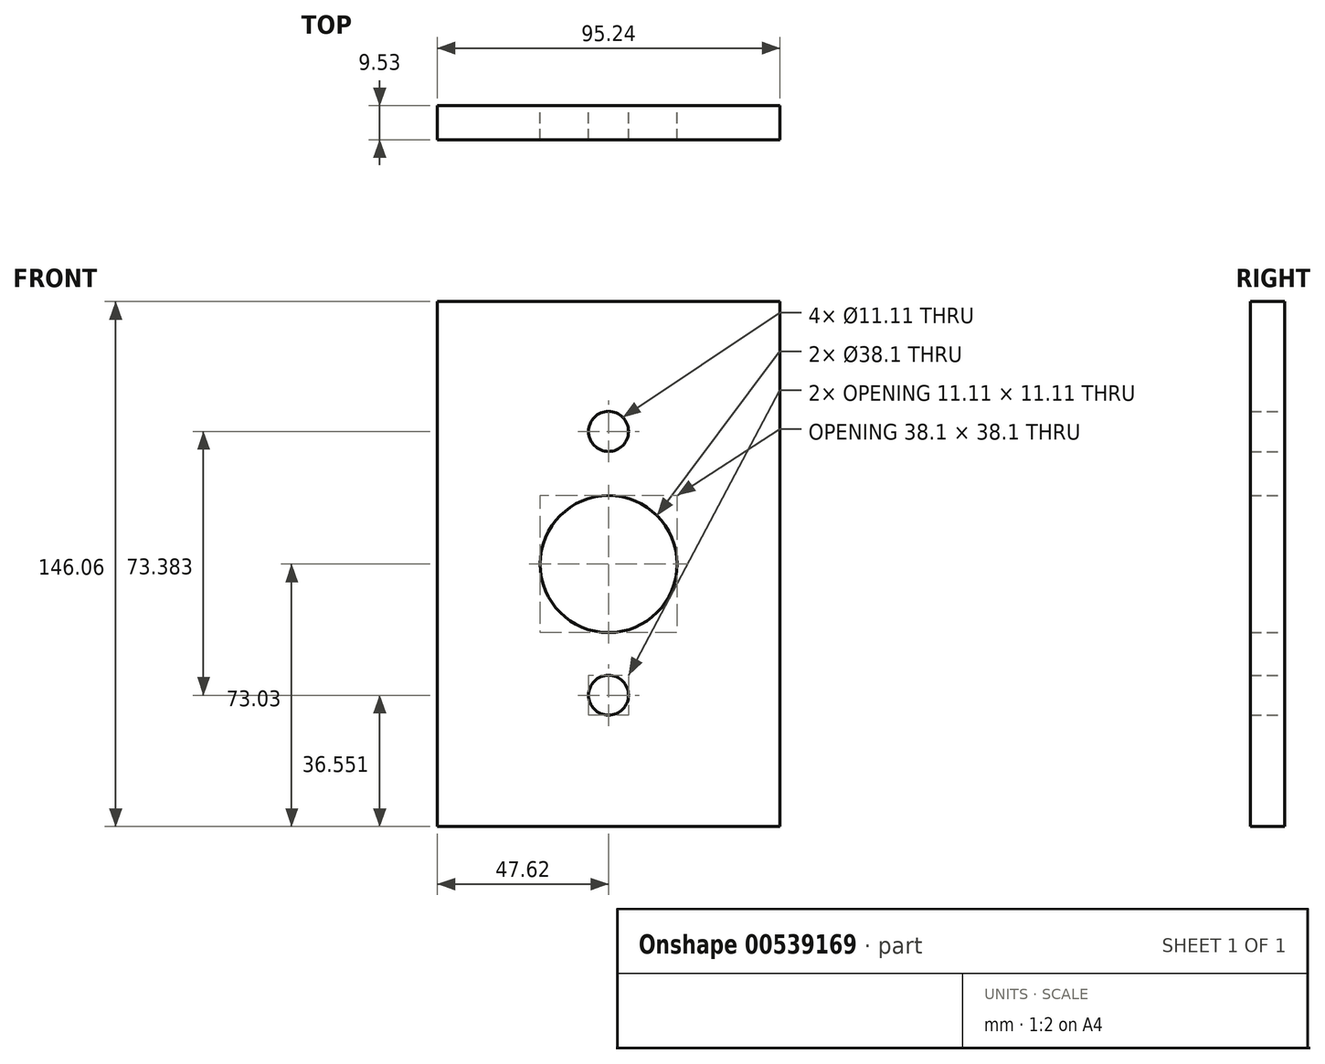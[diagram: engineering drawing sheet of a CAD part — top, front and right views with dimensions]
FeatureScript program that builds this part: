
annotation { "Feature Type Name" : "Feature", "Feature Type Description" : "" }
export const myFeature = defineFeature(function(context is Context, id is Id, definition is map)
    precondition{}
    {
        {
            var Q0;
            Q0=qCreatedBy(makeId("Front.planeOp"),FACE);
            var sketch = newSketch(context, id + "F0", { "sketchPlane" : qUnion([Q0])});
            skCircle(sketch, "E0", {"center": v(0, 0) * mm, "radius": 19.05 * mm});
            skCircle(sketch, "E1", {"center": v(0, 36.9) * mm, "radius": 5.56 * mm});
            skCircle(sketch, "E2", {"center": v(0, -36.48) * mm, "radius": 5.56 * mm});
            skSolve(sketch);
        }
        {
            var Q0;
            Q0=qCreatedBy(makeId("Front.planeOp"),FACE);
            var sketch = newSketch(context, id + "F1", { "sketchPlane" : qUnion([Q0])});
            skLineSegment(sketch, "E3.bottom", {"start": v(-47.62, 73.02) * mm, "end": v(47.63, 73.02) * mm});
            skLineSegment(sketch, "E3.top", {"start": v(-47.63, -73.03) * mm, "end": v(47.62, -73.03) * mm});
            skLineSegment(sketch, "E3.left", {"start": v(-47.62, 73.02) * mm, "end": v(-47.63, -73.03) * mm});
            skLineSegment(sketch, "E3.right", {"start": v(47.63, 73.02) * mm, "end": v(47.62, -73.03) * mm});
            skPoint(sketch, "E3.middle", {"position": v(0, 0) * mm});
            skSolve(sketch);
        }
        {
            var Q0;
            Q0=makeQuery(id+"F1.imprint","IMPRINT",FACE,{"disambiguationData":[TD([[makeQuery(id+"F1.imprint","IMPRINT",EDGE,{"derivedFrom":sQuery(id+"F1.wireOp",EDGE,"E3.bottom")}),-1.0]])]});
            extrude(context, id + "F2", {"entities" : qUnion([Q0]), "depth" : 9.52 * mm, "offsetDistance" : 25.4 * mm});
        }
        {
            var Q0;
            Q0=sQuery(id+"F0.wireOp",VERTEX,"E0.center");
            var Q1;
            Q1=makeQuery(id+"F2.opExtrude","SWEPT_BODY",BODY,{"disambiguationData":[OSD([sQuery(id+"F1.wireOp",EDGE,"E3.bottom"),sQuery(id+"F1.wireOp",EDGE,"E3.top"),sQuery(id+"F1.wireOp",EDGE,"E3.left"),sQuery(id+"F1.wireOp",EDGE,"E3.right")])]});
            hole(context, id + "F3", {"style" : HoleStyle.SIMPLE, "endStyle" : HoleEndStyle.BLIND, "oppositeDirection" : true, "holeDiameter" : 38.1 * mm, "holeDepth" : 12.7 * mm, "isTappedThrough" : true, "tappedDepth" : 12.7 * mm, "tapClearance" : 3, "startFromSketch" : true, "locations" : qUnion([Q0]), "scope" : qUnion([Q1])});
        }
        {
            var Q0;
            Q0=sQuery(id+"F0.wireOp",VERTEX,"E1.center");
            var Q1;
            Q1=makeQuery(id+"F2.opExtrude","SWEPT_BODY",BODY,{"disambiguationData":[OSD([sQuery(id+"F1.wireOp",EDGE,"E3.bottom"),sQuery(id+"F1.wireOp",EDGE,"E3.top"),sQuery(id+"F1.wireOp",EDGE,"E3.left"),sQuery(id+"F1.wireOp",EDGE,"E3.right")])]});
            hole(context, id + "F4", {"style" : HoleStyle.SIMPLE, "endStyle" : HoleEndStyle.THROUGH, "oppositeDirection" : true, "holeDiameter" : 11.1 * mm, "isTappedThrough" : true, "tappedDepth" : 12.7 * mm, "tapClearance" : 3, "locations" : qUnion([Q0]), "scope" : qUnion([Q1])});
        }
        {
            var Q0;
            Q0=sQuery(id+"F0.wireOp",VERTEX,"E2.center");
            var Q1;
            Q1=makeQuery(id+"F2.opExtrude","SWEPT_BODY",BODY,{"disambiguationData":[OSD([sQuery(id+"F1.wireOp",EDGE,"E3.bottom"),sQuery(id+"F1.wireOp",EDGE,"E3.top"),sQuery(id+"F1.wireOp",EDGE,"E3.left"),sQuery(id+"F1.wireOp",EDGE,"E3.right")])]});
            hole(context, id + "F5", {"style" : HoleStyle.SIMPLE, "endStyle" : HoleEndStyle.THROUGH, "oppositeDirection" : true, "holeDiameter" : 11.1 * mm, "isTappedThrough" : true, "tappedDepth" : 12.7 * mm, "tapClearance" : 3, "locations" : qUnion([Q0]), "scope" : qUnion([Q1])});
        }
    });
